FCSTD DOCUMENT  (FreeCAD 0.20R29382 +95 (Git))
Label: pump-crane-plants
License: All rights reserved
LicenseURL: http://en.wikipedia.org/wiki/All_rights_reserved
objects: Sketcher::SketchObject×1, PartDesign::Body×1
note: 2 computed .brp shape members not serialized (recipe doc carries the construction recipe); baked Part::Feature solids carry a one-line shape summary decoded from their .brp

FEATURE [Sketcher::SketchObject] Sketch
  FullyConstrained = true
  MapMode = 5
  Support = -> [XY_Plane]
  expr: Constraints[220] = .Constraints.WateringRadius - 20mm
  expr: Constraints[96] = .Constraints.OuterDiameter - 100mm
  sketch-geometry (95):
    g0: Circle CenterX=0 CenterY=0 CenterZ=0 NormalX=0 NormalY=0 NormalZ=1 AngleXU=0 Radius=305
    g1: Circle CenterX=-208.435 CenterY=-15.3508 CenterZ=0 NormalX=0 NormalY=0 NormalZ=1 AngleXU=0 Radius=46
    g2: Circle CenterX=-174.337 CenterY=115.272 CenterZ=0 NormalX=0 NormalY=0 NormalZ=1 AngleXU=0 Radius=46
    g3: Circle CenterX=-67.5 CenterY=197.8 CenterZ=0 NormalX=0 NormalY=0 NormalZ=1 AngleXU=0 Radius=46
    g4: Circle CenterX=67.5 CenterY=197.8 CenterZ=0 NormalX=0 NormalY=0 NormalZ=1 AngleXU=0 Radius=46
    g5: Circle CenterX=174.337 CenterY=115.272 CenterZ=0 NormalX=0 NormalY=0 NormalZ=1 AngleXU=0 Radius=46
    g6: Circle CenterX=208.435 CenterY=-15.3508 CenterZ=0 NormalX=0 NormalY=0 NormalZ=1 AngleXU=0 Radius=46
    g7: Circle CenterX=-91.2392 CenterY=118.114 CenterZ=0 NormalX=0 NormalY=0 NormalZ=1 AngleXU=0 Radius=46
    g8: Circle CenterX=91.2392 CenterY=118.114 CenterZ=0 NormalX=0 NormalY=0 NormalZ=1 AngleXU=0 Radius=46
    g9: Circle CenterX=144.411 CenterY=37.6978 CenterZ=0 NormalX=0 NormalY=0 NormalZ=1 AngleXU=0 Radius=46
    g10: Circle CenterX=-144.411 CenterY=37.6978 CenterZ=0 NormalX=0 NormalY=0 NormalZ=1 AngleXU=0 Radius=46
    g11: LineSegment StartX=-208.435 StartY=-15.3508 StartZ=0 EndX=-144.411 EndY=37.6978 EndZ=0
    g12: LineSegment StartX=-144.411 StartY=37.6978 StartZ=0 EndX=-174.337 EndY=115.272 EndZ=0
    g13: LineSegment StartX=-144.411 StartY=37.6978 StartZ=0 EndX=0 EndY=0 EndZ=0
    g14: GeomPoint X=-99.9022 Y=26.079 Z=0
    g15: LineSegment StartX=-208.435 StartY=-15.3508 StartZ=0 EndX=0 EndY=0 EndZ=0
    g16: LineSegment StartX=0 StartY=0 StartZ=0 EndX=-174.337 EndY=115.272 EndZ=0
    g17: LineSegment StartX=-67.5 StartY=197.8 StartZ=0 EndX=0 EndY=0 EndZ=0
    g18: LineSegment StartX=67.5 StartY=197.8 StartZ=0 EndX=0 EndY=0 EndZ=0
    g19: LineSegment StartX=174.337 StartY=115.272 StartZ=0 EndX=0 EndY=1.42e-14 EndZ=0
    g20: LineSegment StartX=144.411 StartY=37.6978 StartZ=0 EndX=0 EndY=0 EndZ=0
    g21: LineSegment StartX=-91.2392 StartY=118.114 StartZ=0 EndX=0 EndY=0 EndZ=0
    g22: LineSegment StartX=91.2392 StartY=118.114 StartZ=0 EndX=0 EndY=0 EndZ=0
    g23: LineSegment StartX=-144.411 StartY=37.6978 StartZ=0 EndX=-91.2392 EndY=118.114 EndZ=0
    g24: Circle CenterX=0 CenterY=149.25 CenterZ=0 NormalX=0 NormalY=0 NormalZ=1 AngleXU=0 Radius=46
    g25: LineSegment StartX=0 StartY=149.25 StartZ=0 EndX=0 EndY=0 EndZ=0
    g26: LineSegment StartX=-91.2392 StartY=118.114 StartZ=0 EndX=0 EndY=149.25 EndZ=0
    g27: LineSegment StartX=0 StartY=149.25 StartZ=0 EndX=91.2392 EndY=118.114 EndZ=0
    g28: LineSegment StartX=91.2392 StartY=118.114 StartZ=0 EndX=144.411 EndY=37.6978 EndZ=0
    g29: LineSegment StartX=-208.435 StartY=-15.3508 StartZ=0 EndX=-174.337 EndY=115.272 EndZ=0
    g30: LineSegment StartX=-174.337 StartY=115.272 StartZ=0 EndX=-67.5 EndY=197.8 EndZ=0
    g31: LineSegment StartX=-67.5 StartY=197.8 StartZ=0 EndX=67.5 EndY=197.8 EndZ=0
    g32: LineSegment StartX=67.5 StartY=197.8 StartZ=0 EndX=174.337 EndY=115.272 EndZ=0
    g33: LineSegment StartX=174.337 StartY=115.272 StartZ=0 EndX=208.435 EndY=-15.3508 EndZ=0
    g34: Circle CenterX=0 CenterY=0 CenterZ=0 NormalX=0 NormalY=0 NormalZ=1 AngleXU=0 Radius=100
    g35: ArcOfCircle CenterX=0 CenterY=-86 CenterZ=0 NormalX=0 NormalY=0 NormalZ=1 AngleXU=0 Radius=86 StartAngle=0 EndAngle=3.14159
    g36: ArcOfCircle CenterX=4.1e-15 CenterY=-204 CenterZ=0 NormalX=0 NormalY=0 NormalZ=1 AngleXU=0 Radius=86 StartAngle=3.14159 EndAngle=6.28319
    g37: LineSegment StartX=-86 StartY=-86 StartZ=0 EndX=-86 EndY=-204 EndZ=0
    g38: LineSegment StartX=86 StartY=-204 StartZ=0 EndX=86 EndY=-86 EndZ=0
    g39: GeomPoint X=0 Y=-290 Z=0
    g40: ArcOfCircle CenterX=0 CenterY=-86 CenterZ=0 NormalX=0 NormalY=0 NormalZ=1 AngleXU=0 Radius=106 StartAngle=0 EndAngle=3.14159
    g41: ArcOfCircle CenterX=4.1e-15 CenterY=-204 CenterZ=0 NormalX=0 NormalY=0 NormalZ=1 AngleXU=0 Radius=106 StartAngle=3.14159 EndAngle=6.28319
    g42: LineSegment StartX=-106 StartY=-86 StartZ=0 EndX=-106 EndY=-204 EndZ=0
    g43: LineSegment StartX=106 StartY=-204 StartZ=0 EndX=106 EndY=-86 EndZ=0
    g44: Circle CenterX=0 CenterY=0 CenterZ=0 NormalX=0 NormalY=0 NormalZ=1 AngleXU=0 Radius=255
    g45: Circle CenterX=-208.435 CenterY=-15.3508 CenterZ=0 NormalX=0 NormalY=0 NormalZ=1 AngleXU=0 Radius=64.25
    g46: Circle CenterX=-144.411 CenterY=37.6978 CenterZ=0 NormalX=0 NormalY=0 NormalZ=1 AngleXU=0 Radius=64.25
    g47: Circle CenterX=-174.337 CenterY=115.272 CenterZ=0 NormalX=0 NormalY=0 NormalZ=1 AngleXU=0 Radius=64.25
    g48: Circle CenterX=-91.2392 CenterY=118.114 CenterZ=0 NormalX=0 NormalY=0 NormalZ=1 AngleXU=0 Radius=64.25
    g49: Circle CenterX=-67.5 CenterY=197.8 CenterZ=0 NormalX=0 NormalY=0 NormalZ=1 AngleXU=0 Radius=64.25
    g50: Circle CenterX=0 CenterY=149.25 CenterZ=0 NormalX=0 NormalY=0 NormalZ=1 AngleXU=0 Radius=64.25
    g51: Circle CenterX=67.5 CenterY=197.8 CenterZ=0 NormalX=0 NormalY=0 NormalZ=1 AngleXU=0 Radius=64.25
    g52: Circle CenterX=91.2392 CenterY=118.114 CenterZ=0 NormalX=0 NormalY=0 NormalZ=1 AngleXU=0 Radius=64.25
    g53: Circle CenterX=174.337 CenterY=115.272 CenterZ=0 NormalX=0 NormalY=0 NormalZ=1 AngleXU=0 Radius=64.25
    g54: Circle CenterX=144.411 CenterY=37.6978 CenterZ=0 NormalX=0 NormalY=0 NormalZ=1 AngleXU=0 Radius=64.25
    g55: Circle CenterX=208.435 CenterY=-15.3508 CenterZ=0 NormalX=0 NormalY=0 NormalZ=1 AngleXU=0 Radius=64.25
    g56: GeomPoint X=-96.7576 Y=25.2581 Z=0
    g57: GeomPoint X=-82.2439 Y=21.4694 Z=0
    g58: LineSegment StartX=-144.359 StartY=-10.6317 StartZ=0 EndX=-120.743 EndY=79.8354 EndZ=0
    g59: LineSegment StartX=-120.743 StartY=79.8354 StartZ=0 EndX=-46.7494 EndY=136.993 EndZ=0
    g60: LineSegment StartX=-46.7494 StartY=136.993 StartZ=0 EndX=46.7494 EndY=136.993 EndZ=0
    g61: LineSegment StartX=46.7494 StartY=136.993 StartZ=0 EndX=120.743 EndY=79.8354 EndZ=0
    g62: LineSegment StartX=120.743 StartY=79.8354 StartZ=0 EndX=144.359 EndY=-10.6317 EndZ=0
    g63: LineSegment StartX=144.359 StartY=-10.6317 StartZ=0 EndX=125.008 EndY=-15.6834 EndZ=0
    g64: LineSegment StartX=125.008 StartY=-15.6834 StartZ=0 EndX=103.115 EndY=68.18 EndZ=0
    g65: LineSegment StartX=103.115 StartY=68.18 StartZ=0 EndX=39.9243 EndY=116.993 EndZ=0
    g66: LineSegment StartX=39.9243 StartY=116.993 StartZ=0 EndX=-39.9243 EndY=116.993 EndZ=0
    g67: LineSegment StartX=-39.9243 StartY=116.993 StartZ=0 EndX=-103.115 EndY=68.18 EndZ=0
    g68: LineSegment StartX=-125.008 StartY=-15.6834 StartZ=0 EndX=-144.359 EndY=-10.6317 EndZ=0
    g69: LineSegment StartX=-103.115 StartY=68.18 StartZ=0 EndX=-125.008 EndY=-15.6834 EndZ=0
    g70: GeomPoint X=-119.04 Y=76.0686 Z=0
    g71: GeomPoint X=-116.61 Y=79.7434 Z=0
    g72: LineSegment StartX=-131.73 StartY=37.7465 StartZ=0 EndX=-190.565 EndY=53.1051 EndZ=0
    g73: GeomPoint X=-192.207 Y=46.8159 Z=0
    g74: GeomPoint X=-185.956 Y=70.7634 Z=0
    g75: GeomPoint X=-196.817 Y=29.1576 Z=0
    g76: LineSegment StartX=-144.359 StartY=-10.6317 StartZ=0 EndX=-154.699 EndY=-50.2422 EndZ=0
    g77: LineSegment StartX=-154.699 StartY=-50.2422 StartZ=0 EndX=-131.891 EndY=-42.0513 EndZ=0
    g78: LineSegment StartX=-131.891 StartY=-42.0513 StartZ=0 EndX=-125.008 EndY=-15.6834 EndZ=0
    g79: LineSegment StartX=-154.699 StartY=-50.2422 StartZ=0 EndX=-241.638 EndY=-81.4631 EndZ=0
    g80: LineSegment StartX=-241.638 StartY=-81.4631 StartZ=0 EndX=-238.258 EndY=-90.8746 EndZ=0
    g81: LineSegment StartX=-154.699 StartY=-50.2422 StartZ=0 EndX=-135.348 EndY=-55.2938 EndZ=0
    g82: LineSegment StartX=-135.348 StartY=-55.2938 StartZ=0 EndX=-131.891 EndY=-42.0513 EndZ=0
    g83: LineSegment StartX=-107.119 StartY=52.8446 StartZ=0 EndX=-94.7055 EndY=44.637 EndZ=0
    g84: LineSegment StartX=-94.7055 StartY=44.637 StartZ=0 EndX=-78.1593 EndY=69.6614 EndZ=0
    g85: LineSegment StartX=-78.1593 StartY=69.6614 StartZ=0 EndX=-90.5724 EndY=77.869 EndZ=0
    g86: LineSegment StartX=-158.053 StartY=165.759 StartZ=0 EndX=-67.7008 EndY=48.792 EndZ=0
    g87: LineSegment StartX=-67.7008 StartY=48.792 StartZ=0 EndX=-30.11 EndY=77.8296 EndZ=0
    g88: LineSegment StartX=-30.11 StartY=77.8296 StartZ=0 EndX=-120.463 EndY=194.796 EndZ=0
    g89: LineSegment StartX=-120.463 StartY=194.796 StartZ=0 EndX=-158.053 EndY=165.759 EndZ=0
    g90: LineSegment StartX=0 StartY=0 StartZ=0 EndX=-239.994 EndY=-86.1855 EndZ=0
    g91: LineSegment StartX=-192.888 StartY=-58.6439 StartZ=0 EndX=-191.198 EndY=-63.3496 EndZ=0
    g92: LineSegment StartX=-238.258 StartY=-90.8746 StartZ=0 EndX=-134.951 EndY=-53.7757 EndZ=0
    g93: LineSegment StartX=-134.951 StartY=-53.7757 StartZ=0 EndX=-131.891 EndY=-42.0513 EndZ=0
    g94: LineSegment StartX=-103.115 StartY=68.18 StartZ=0 EndX=-111.388 EndY=55.6678 EndZ=0
  constraints (246):
    c: Coincident(g0,g-1)
    c: Diameter(g0) = 610  'OuterDiameter'
    c: Equal(g1,g2)
    c: Equal(g2,g3)
    c: Equal(g3,g4)
    c: Equal(g4,g5)
    c: Equal(g5,g6)
    c: Horizontal(g6,g1)
    c: Equal(g9,g8)
    c: Equal(g10,g1)
    c: Equal(g10,g7)
    c: Coincident(g11,g1)
    c: Coincident(g11,g10)
    c: Coincident(g12,g10)
    c: Coincident(g12,g2)
    c: Equal(g12,g11)
    c: Coincident(g13,g10)
    c: PointOnObject(g14,g13)
    c: PointOnObject(g14,g10)
    c: PointOnObject(g13,g-2)
    c: Coincident(g15,g1)
    c: Coincident(g15,g13)
    c: Coincident(g16,g13)
    c: Coincident(g16,g2)
    c: Coincident(g17,g3)
    c: Coincident(g17,g13)
    c: Coincident(g18,g4)
    c: Coincident(g18,g13)
    c: Coincident(g19,g5)
    c: Coincident(g19,g13)
    c: Equal(g15,g16)
    c: Equal(g16,g17)
    c: Equal(g17,g18)
    c: Equal(g18,g19)
    c: Equal(g7,g8)
    c: Horizontal(g9,g10)
    c: Coincident(g20,g9)
    c: Coincident(g20,g13)
    c: Equal(g20,g13)
    c: Coincident(g21,g7)
    c: Coincident(g21,g13)
    c: Coincident(g22,g8)
    c: Coincident(g22,g13)
    c: Equal(g21,g22)
    c: Equal(g22,g20)
    c: Diameter(g1) = 92
    c: Coincident(g23,g10)
    c: Coincident(g23,g7)
    c: Coincident(g25,g24)
    c: Coincident(g25,g13)
    c: Equal(g25,g21)
    c: Equal(g24,g10)
    c: Coincident(g26,g7)
    c: Coincident(g26,g24)
    c: Coincident(g27,g24)
    c: Coincident(g27,g8)
    c: Equal(g27,g26)
    c: Equal(g26,g23)
    c: Coincident(g28,g8)
    c: Coincident(g28,g9)
    c: Equal(g28,g27)
    c: Coincident(g29,g1)
    c: Coincident(g29,g2)
    c: Coincident(g30,g2)
    c: Coincident(g30,g3)
    c: Coincident(g31,g3)
    c: Coincident(g31,g4)
    c: Horizontal(g31)
    c: Coincident(g32,g4)
    c: Coincident(g32,g5)
    c: Coincident(g33,g5)
    c: Coincident(g33,g6)
    c: Equal(g29,g30)
    c: Equal(g30,g31)
    c: Equal(g31,g32)
    c: Coincident(g34,g0)
    c: Tangent(g35,g37) = -1.5708
    c: Tangent(g37,g36) = -1.5708
    c: Tangent(g36,g38) = -1.5708
    c: Tangent(g38,g35) = -1.5708
    c: Equal(g35,g36)
    c: PointOnObject(g35,g-2)
    c: Vertical(g37)
    c: DistanceX(g35,g35) = 172
    c: PointOnObject(g39,g36)
    c: PointOnObject(g39,g-2)
    c: DistanceY(g39,g0) = 290
    c: Tangent(g40,g42) = -1.5708
    c: Tangent(g42,g41) = -1.5708
    c: Tangent(g41,g43) = -1.5708
    c: Tangent(g43,g40) = -1.5708
    c: Equal(g40,g41)
    c: Coincident(g40,g35)
    c: Coincident(g41,g36)
    c: DistanceX(g36,g41) = 20
    c: Coincident(g44,g0)
    c: Diameter(g44) = 510
    c: PointOnObject(g0,g35)
    c: Tangent(g1,g44)
    c: Tangent(g6,g44)
    c: Tangent(g3,g44)
    c: Coincident(g45,g1)
    c: Coincident(g46,g10)
    c: Coincident(g47,g2)
    c: Coincident(g48,g7)
    c: Coincident(g49,g3)
    c: Coincident(g50,g24)
    c: Coincident(g51,g4)
    c: Coincident(g52,g8)
    c: Coincident(g53,g5)
    c: Coincident(g54,g9)
    c: Coincident(g55,g6)
    c: Equal(g45,g47)
    c: Equal(g47,g49)
    c: Equal(g49,g51)
    c: Equal(g51,g53)
    c: Equal(g53,g55)
    c: Equal(g46,g48)
    c: Equal(g48,g50)
    c: Equal(g50,g52)
    c: Equal(g52,g54)
    c: Equal(g46,g45)
    c: Diameter(g45) = 128.5
    c: PointOnObject(g56,g34)
    c: PointOnObject(g57,g46)
    c: PointOnObject(g56,g13)
    c: PointOnObject(g57,g13)
    c: Distance(g57,g56) = 15
    c: Radius(g34) = 100  'WateringRadius'
    c: PointOnObject(g58,g45)
    c: PointOnObject(g58,g47)
    c: Coincident(g58,g59)
    c: PointOnObject(g59,g49)
    c: Coincident(g59,g60)
    c: PointOnObject(g60,g51)
    c: Coincident(g60,g61)
    c: PointOnObject(g61,g53)
    c: Coincident(g61,g62)
    c: PointOnObject(g62,g55)
    c: Coincident(g62,g63)
    c: Coincident(g63,g64)
    c: Coincident(g64,g65)
    c: Coincident(g65,g66)
    c: Coincident(g66,g67)
    c: Coincident(g68,g58)
    c: Parallel(g67,g59)
    c: Parallel(g66,g60)
    c: Parallel(g65,g61)
    c: Parallel(g64,g62)
    c: Perpendicular(g64,g63)
    c: Equal(g62,g61)
    c: Equal(g61,g60)
    c: Equal(g60,g59)
    c: Equal(g59,g58)
    c: PointOnObject(g58,g16)
    c: PointOnObject(g67,g16)
    c: PointOnObject(g66,g17)
    c: PointOnObject(g65,g18)
    c: Coincident(g69,g67)
    c: Coincident(g69,g68)
    c: Parallel(g69,g58)
    c: Perpendicular(g58,g68)
    c: PointOnObject(g64,g19)
    c: Distance(g68) = 20
    c: PointOnObject(g70,g10)
    c: PointOnObject(g71,g7)
    c: PointOnObject(g70,g23)
    c: PointOnObject(g71,g23)
    c: Distance(g70,g71) = 4.4055
    c: PointOnObject(g72,g58)
    c: PointOnObject(g72,g47)
    c: Tangent(g72,g47)
    c: Perpendicular(g58,g72)
    c: Distance(g72) = 60.8069
    c: PointOnObject(g73,g29)
    c: PointOnObject(g73,g45)
    c: Distance(g73,g72) = 6.5
    c: PointOnObject(g74,g29)
    c: PointOnObject(g75,g29)
    c: PointOnObject(g75,g1)
    c: PointOnObject(g74,g2)
    c: Distance(g75,g74) = 43
    c: Coincident(g58,g76)
    c: Coincident(g76,g77)
    c: Coincident(g77,g78)
    c: Coincident(g78,g68)
    c: Parallel(g78,g69)
    c: Parallel(g76,g58)
    c: Coincident(g79,g80)
    c: PointOnObject(g79,g44)
    c: Distance(g80) = 10
    c: Distance(g59) = 93.4988
    c: Distance(g67) = 79.8486
    c: PointOnObject(g58,g15)
    c: Coincident(g76,g81)
    c: Coincident(g81,g82)
    c: Coincident(g82,g77)
    c: Parallel(g82,g78)
    c: Perpendicular(g82,g81)
    c: Distance(g81,g67) = 127.612
    c: Distance(g76,g58) = 134.437
    c: Distance(g77,g67) = 113.925
    c: Distance(g74,g58) = 60.8069
    c: PointOnObject(g83,g69)
    c: Coincident(g83,g84)
    c: Coincident(g84,g85)
    c: Symmetric(g83,g85,g16)
    c: Symmetric(g83,g84,g16)
    c: Perpendicular(g85,g84)
    c: Distance(g84) = 30
    c: Distance(g67,g84) = 20
    c: Coincident(g86,g87)
    c: Coincident(g87,g88)
    c: Coincident(g88,g89)
    c: Coincident(g89,g86)
    c: Perpendicular(g88,g89)
    c: Perpendicular(g87,g86)
    c: Parallel(g86,g88)
    c: Distance(g87) = 47.5
    c: Symmetric(g87,g86,g21)
    c: Distance(g0,g87) = 80
    c: Distance(g2,g89) = 30
    c: Distance(g88) = 147.8
    c: Coincident(g79,g76)
    c: Parallel(g79,g77)
    c: Coincident(g90,g0)
    c: PointOnObject(g90,g44)
    c: Symmetric(g80,g79,g90)
    c: Perpendicular(g80,g79)
    c: PointOnObject(g91,g1)
    c: PointOnObject(g91,g79)
    c: Perpendicular(g79,g91)
    c: PointOnObject(g1,g91)
    c: Distance(g91) = 5
    c: Coincident(g80,g92)
    c: PointOnObject(g92,g82)
    c: Coincident(g92,g93)
    c: Coincident(g93,g77)
    c: Parallel(g92,g79)
    c: Distance(g77,g79) = 116.609
    c: Angle(g69,g67) = 2.48387
    c: Angle(g69,g83) = 1.24193
    c: Coincident(g94,g67)
    c: PointOnObject(g94,g83)
    c: Parallel(g94,g84)
    c: Distance(g94,g83) = 5.11881
FEATURE [PartDesign::Body] Body
  Group = -> [Sketch]
  Origin = -> Origin
